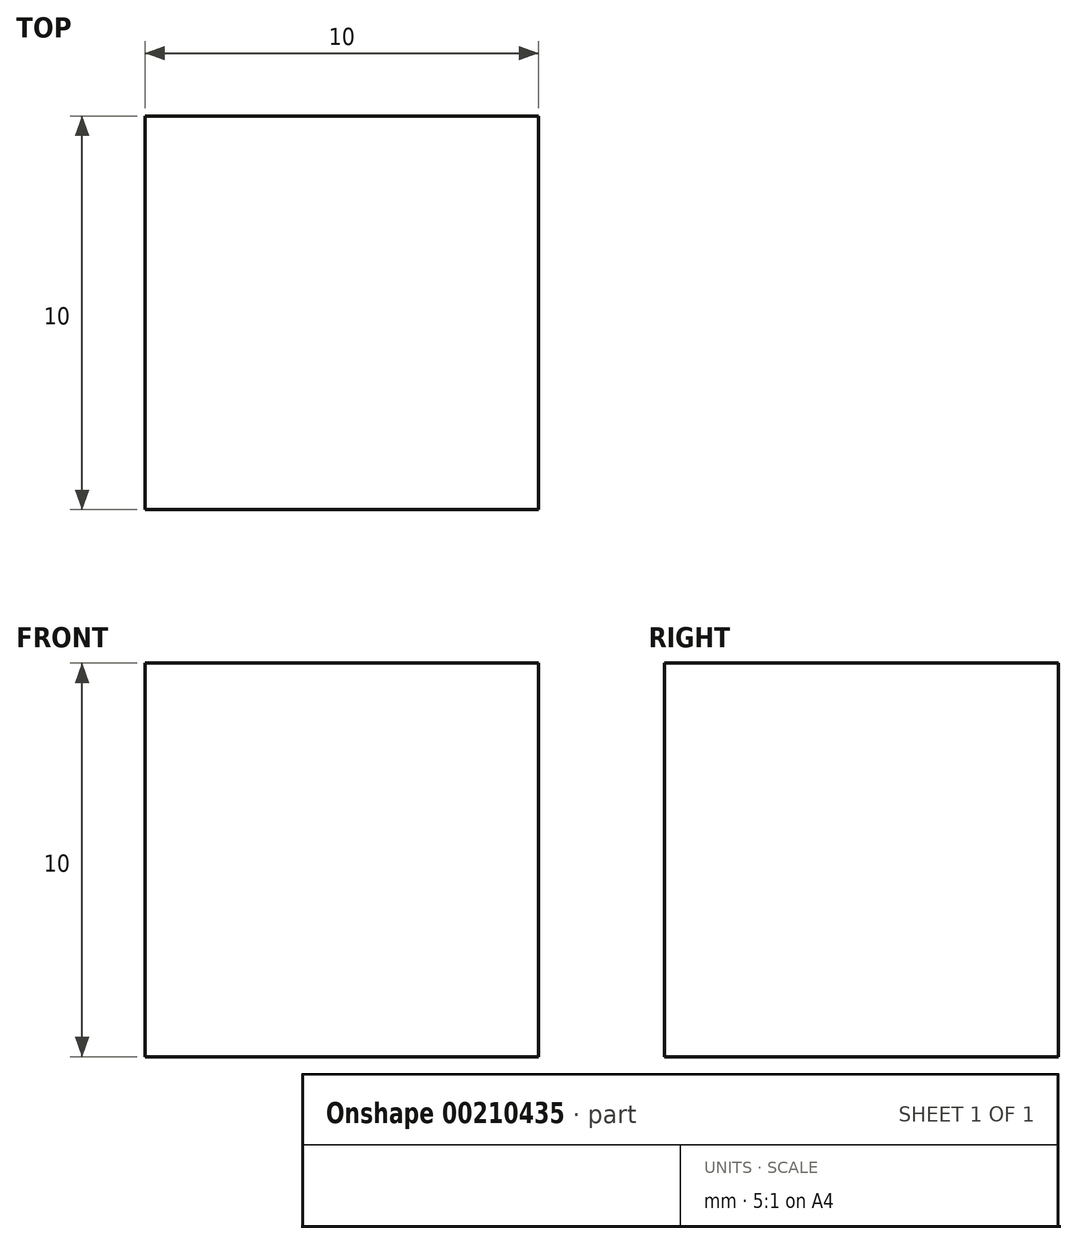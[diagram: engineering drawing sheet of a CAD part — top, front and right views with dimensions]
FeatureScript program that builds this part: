
annotation { "Feature Type Name" : "Feature", "Feature Type Description" : "" }
export const myFeature = defineFeature(function(context is Context, id is Id, definition is map)
    precondition{}
    {
        {
            var Q0;
            Q0=qCreatedBy(makeId("Top.planeOp"),FACE);
            var sketch = newSketch(context, id + "F0", { "sketchPlane" : qUnion([Q0])});
            skLineSegment(sketch, "E0.bottom", {"start": v(-5, 5) * mm, "end": v(5, 5) * mm});
            skLineSegment(sketch, "E0.top", {"start": v(-5, -5) * mm, "end": v(5, -5) * mm});
            skLineSegment(sketch, "E0.left", {"start": v(-5, 5) * mm, "end": v(-5, -5) * mm});
            skLineSegment(sketch, "E0.right", {"start": v(5, 5) * mm, "end": v(5, -5) * mm});
            skPoint(sketch, "E0.middle", {"position": v(0, 0) * mm});
            skSolve(sketch);
        }
        {
            var Q0;
            Q0 = qSketchRegion(id + "F0", true);
            extrude(context, id + "F1", {"entities" : qUnion([Q0]), "depth" : 10 * mm});
        }
    });
